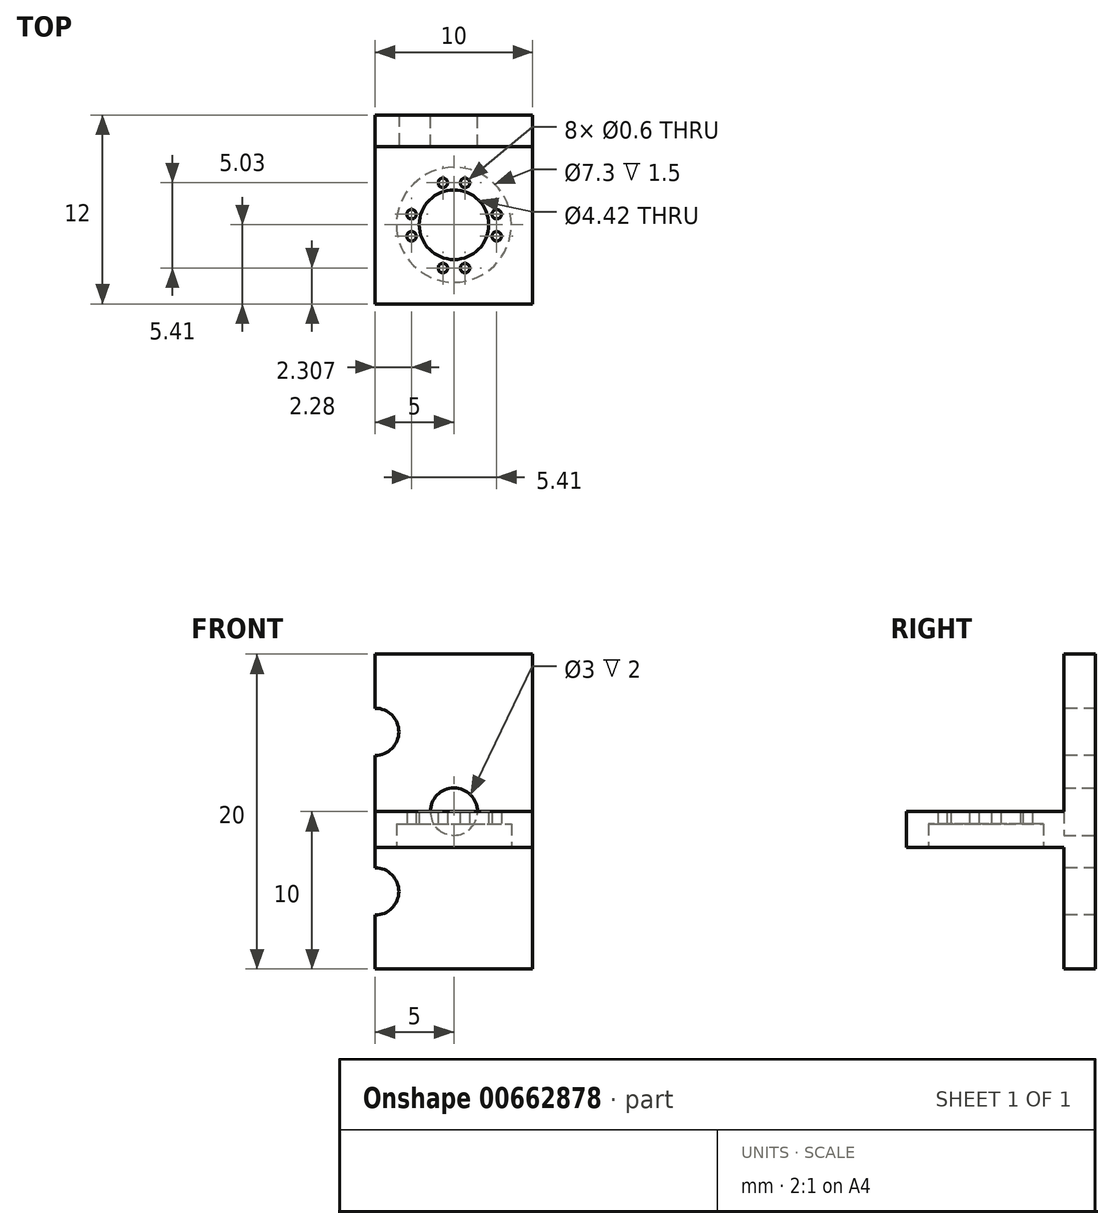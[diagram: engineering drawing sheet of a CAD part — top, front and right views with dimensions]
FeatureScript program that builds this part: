
annotation { "Feature Type Name" : "Feature", "Feature Type Description" : "" }
export const myFeature = defineFeature(function(context is Context, id is Id, definition is map)
    precondition{}
    {
        {
            var Q0;
            Q0=qCreatedBy(makeId("Front.planeOp"),FACE);
            var sketch = newSketch(context, id + "F0", { "sketchPlane" : qUnion([Q0])});
            skLineSegment(sketch, "E0.bottom", {"start": v(-5, 10) * mm, "end": v(5, 10) * mm});
            skLineSegment(sketch, "E0.top", {"start": v(-5, -10) * mm, "end": v(5, -10) * mm});
            skLineSegment(sketch, "E0.left", {"start": v(-5, 10) * mm, "end": v(-5, -10) * mm});
            skLineSegment(sketch, "E0.right", {"start": v(5, 10) * mm, "end": v(5, -10) * mm});
            skPoint(sketch, "E0.middle", {"position": v(0, 0) * mm});
            skSolve(sketch);
        }
        {
            var Q0;
            Q0 = qSketchRegion(id + "F0", true);
            extrude(context, id + "F1", {"entities" : qUnion([Q0]), "depth" : 2 * mm, "offsetDistance" : 25.4 * mm});
        }
        {
            var Q0;
            Q0=makeQuery(id+"F1.opExtrude","CAP_FACE",FACE,{"disambiguationData":[OSD([sQuery(id+"F0.wireOp",EDGE,"E0.bottom"),sQuery(id+"F0.wireOp",EDGE,"E0.top"),sQuery(id+"F0.wireOp",EDGE,"E0.left"),sQuery(id+"F0.wireOp",EDGE,"E0.right")])],"isStart":false});
            var sketch = newSketch(context, id + "F2", { "sketchPlane" : qUnion([Q0])});
            skCircle(sketch, "E1", {"center": v(-5, 5.07) * mm, "radius": 1.5 * mm});
            skCircle(sketch, "E2.MirrorC", {"center": v(-5, -5.07) * mm, "radius": 1.5 * mm});
            skSolve(sketch);
        }
        {
            var Q0;
            Q0 = qSketchRegion(id + "F2", true);
            extrude(context, id + "F3", {"entities" : qUnion([Q0]), "operationType" : NewBodyOperationType.REMOVE, "oppositeDirection" : true, "depth" : 25.4 * mm, "offsetDistance" : 25.4 * mm});
        }
        {
            var Q0;
            Q0=makeQuery(id+"F1.opExtrude","CAP_FACE",FACE,{"disambiguationData":[OSD([sQuery(id+"F0.wireOp",EDGE,"E0.bottom"),sQuery(id+"F0.wireOp",EDGE,"E0.top"),sQuery(id+"F0.wireOp",EDGE,"E0.left"),sQuery(id+"F0.wireOp",EDGE,"E0.right")])],"isStart":false});
            var sketch = newSketch(context, id + "F4", { "sketchPlane" : qUnion([Q0])});
            skLineSegment(sketch, "E3.bottom", {"start": v(-5, 0) * mm, "end": v(5, 0) * mm});
            skLineSegment(sketch, "E3.top", {"start": v(-5, -2.27) * mm, "end": v(5, -2.27) * mm});
            skLineSegment(sketch, "E3.left", {"start": v(-5, 0) * mm, "end": v(-5, -2.27) * mm});
            skLineSegment(sketch, "E3.right", {"start": v(5, 0) * mm, "end": v(5, -2.27) * mm});
            skSolve(sketch);
        }
        {
            var Q0;
            Q0 = qSketchRegion(id + "F4", true);
            extrude(context, id + "F5", {"entities" : qUnion([Q0]), "operationType" : NewBodyOperationType.ADD, "depth" : 10 * mm, "offsetDistance" : 25.4 * mm});
        }
        {
            var Q0;
            Q0=makeQuery(id+"F1.opExtrude","CAP_FACE",FACE,{"disambiguationData":[OSD([sQuery(id+"F0.wireOp",EDGE,"E0.bottom"),sQuery(id+"F0.wireOp",EDGE,"E0.top"),sQuery(id+"F0.wireOp",EDGE,"E0.left"),sQuery(id+"F0.wireOp",EDGE,"E0.right")])],"isStart":true});
            var sketch = newSketch(context, id + "F6", { "sketchPlane" : qUnion([Q0])});
            skCircle(sketch, "E4", {"center": v(0, 0) * mm, "radius": 1.5 * mm});
            skSolve(sketch);
        }
        {
            var Q0;
            Q0 = qSketchRegion(id + "F6", true);
            extrude(context, id + "F7", {"entities" : qUnion([Q0]), "operationType" : NewBodyOperationType.REMOVE, "oppositeDirection" : true, "depth" : 2 * mm, "offsetDistance" : 25.4 * mm});
        }
        {
            var Q0;
            Q0=makeQuery(id+"F5.opExtrude","SWEPT_FACE",FACE,{"disambiguationData":[OSD([sQuery(id+"F4.wireOp",EDGE,"E3.top")])]});
            var sketch = newSketch(context, id + "F8", { "sketchPlane" : qUnion([Q0])});
            skCircle(sketch, "E5", {"center": v(0, 6.97) * mm, "radius": 3.65 * mm});
            skSolve(sketch);
        }
        {
            var Q0;
            Q0 = qSketchRegion(id + "F8", true);
            extrude(context, id + "F9", {"entities" : qUnion([Q0]), "operationType" : NewBodyOperationType.REMOVE, "oppositeDirection" : true, "depth" : 1.5 * mm, "offsetDistance" : 25.4 * mm});
        }
        {
            var Q0;
            Q0=makeQuery(id+"F9.boolean.opBoolean","COPY",FACE,{"derivedFrom":makeQuery(id+"F9.opExtrude","CAP_FACE",FACE,{"disambiguationData":[OSD([sQuery(id+"F8.wireOp",EDGE,"E5")])],"isStart":false})});
            var sketch = newSketch(context, id + "F10", { "sketchPlane" : qUnion([Q0])});
            skCircle(sketch, "E6", {"center": v(0, 6.97) * mm, "radius": 2.21 * mm});
            skSolve(sketch);
        }
        {
            var Q0;
            Q0 = qSketchRegion(id + "F10", true);
            extrude(context, id + "F11", {"entities" : qUnion([Q0]), "operationType" : NewBodyOperationType.REMOVE, "oppositeDirection" : true, "depth" : 1 * mm, "offsetDistance" : 25.4 * mm});
        }
        {
            var Q0;
            Q0=makeQuery(id+"F9.boolean.opBoolean","COPY",FACE,{"derivedFrom":makeQuery(id+"F9.opExtrude","CAP_FACE",FACE,{"disambiguationData":[OSD([sQuery(id+"F8.wireOp",EDGE,"E5")])],"isStart":false})});
            var sketch = newSketch(context, id + "F12", { "sketchPlane" : qUnion([Q0])});
            skCircle(sketch, "E7", {"center": v(0.7, 4.3) * mm, "radius": 0.3 * mm});
            skCircle(sketch, "E8.MirrorC", {"center": v(-0.7, 4.3) * mm, "radius": 0.3 * mm});
            skLineSegment(sketch, "E9", {"start": v(5.96, 7.01) * mm, "end": v(-6.95, 7.01) * mm});
            skCircle(sketch, "E10.MirrorC", {"center": v(0.7, 9.72) * mm, "radius": 0.3 * mm});
            skCircle(sketch, "E11.MirrorC", {"center": v(-0.7, 9.72) * mm, "radius": 0.3 * mm});
            skLineSegment(sketch, "E12", {"start": v(4.99, 12) * mm, "end": v(-4.98, 2.02) * mm});
            skCircle(sketch, "E13.MirrorC", {"center": v(-2.7, 6.3) * mm, "radius": 0.3 * mm});
            skCircle(sketch, "E14.MirrorC", {"center": v(-2.7, 7.7) * mm, "radius": 0.3 * mm});
            skCircle(sketch, "E15.MirrorC", {"center": v(2.72, 6.3) * mm, "radius": 0.3 * mm});
            skCircle(sketch, "E16.MirrorC", {"center": v(2.72, 7.7) * mm, "radius": 0.3 * mm});
            skSolve(sketch);
        }
        {
            var Q0;
            Q0 = qSketchRegion(id + "F12", true);
            extrude(context, id + "F13", {"entities" : qUnion([Q0]), "operationType" : NewBodyOperationType.REMOVE, "oppositeDirection" : true, "depth" : 1 * mm, "offsetDistance" : 25.4 * mm});
        }
    });
